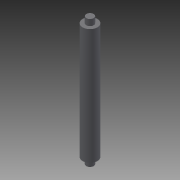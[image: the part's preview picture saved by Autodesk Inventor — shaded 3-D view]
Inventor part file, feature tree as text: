
AUTODESK INVENTOR PART (.ipt)
format: ipt  version: 2014 (Build 180170000, 170)  size: 101,376 bytes
history: native  units: in
note: dims shown in document units (in); Inventor stores cm internally (conversion verified against a paired STEP export)
features: other x7, revolve x3, sketch x3
ambient origin geometry x8: Origin, YZ Plane, XZ Plane, XY Plane, X Axis, Y Axis, Z Axis, Center Point
bodies: Solid1 (feature_tree)
feature tree (13):
  revolve  "Revolution1"  Angle=360.0deg
  revolve  "Revolution2"  [1 undecoded]
  revolve  "Revolution3"  [1 undecoded]
  other  "additional_rod_XY"
  other  "additional_rod_YZ"
  other  "additional_rod_ZX"
  other  "additional_rod_X"
  other  "additional_rod_Y"
  other  "additional_rod_Z"
  other  "additional_rod_Center"
  sketch  "Sketch_1"  dims[d0=360.0deg d1=360.0deg]
  sketch  "Sketch_3"  dims[d2=360.0deg]
  sketch  "Sketch_4"
note: 2 required parameter values undecoded (feature->parameter linkage not recoverable at this tier; creation-order binding heuristic only, values carry confidence <= 0.55)
